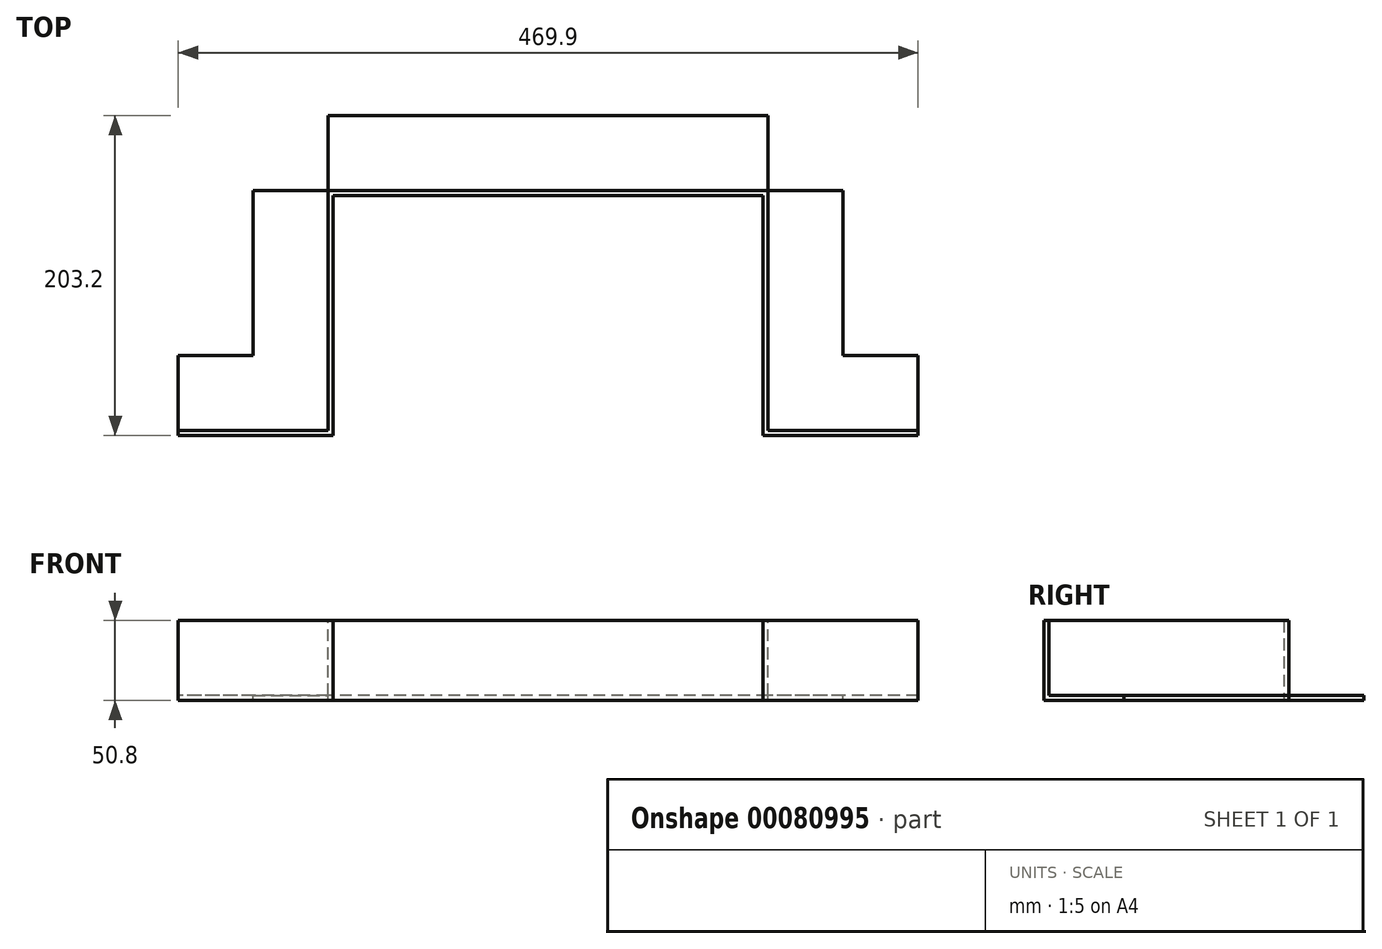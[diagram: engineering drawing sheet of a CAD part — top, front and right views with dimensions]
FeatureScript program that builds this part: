
annotation { "Feature Type Name" : "Feature", "Feature Type Description" : "" }
export const myFeature = defineFeature(function(context is Context, id is Id, definition is map)
    precondition{}
    {
        {
            var Q0;
            Q0=qCreatedBy(makeId("Right.planeOp"),FACE);
            var sketch = newSketch(context, id + "F0", { "sketchPlane" : qUnion([Q0])});
            skLineSegment(sketch, "E0", {"start": v(0, 0) * mm, "end": v(50.8, 0) * mm});
            skLineSegment(sketch, "E1", {"start": v(50.8, 0) * mm, "end": v(50.8, 3.18) * mm});
            skLineSegment(sketch, "E2", {"start": v(50.8, 3.18) * mm, "end": v(3.18, 3.17) * mm});
            skLineSegment(sketch, "E3", {"start": v(3.17, 3.17) * mm, "end": v(3.17, 50.8) * mm});
            skLineSegment(sketch, "E4", {"start": v(3.17, 50.8) * mm, "end": v(0, 50.8) * mm});
            skLineSegment(sketch, "E5", {"start": v(0, 50.8) * mm, "end": v(0, 0) * mm});
            skSolve(sketch);
        }
        {
            var Q0;
            Q0=qCreatedBy(makeId("Top.planeOp"),FACE);
            var sketch = newSketch(context, id + "F1", { "sketchPlane" : qUnion([Q0])});
            skLineSegment(sketch, "E6", {"start": v(0, 0) * mm, "end": v(-98.43, 0) * mm});
            skLineSegment(sketch, "E7", {"start": v(-98.43, 0) * mm, "end": v(-98.43, 152.4) * mm});
            skLineSegment(sketch, "E8", {"start": v(-98.43, 152.4) * mm, "end": v(-371.47, 152.4) * mm});
            skLineSegment(sketch, "E9", {"start": v(-371.47, 152.4) * mm, "end": v(-371.47, 0) * mm});
            skLineSegment(sketch, "E10", {"start": v(-371.47, 0) * mm, "end": v(-469.9, 0) * mm});
            skSolve(sketch);
        }
        {
            var Q0;
            Q0=makeQuery(id+"F0.imprint","IMPRINT",FACE,{"disambiguationData":[TD([[makeQuery(id+"F0.imprint","IMPRINT",EDGE,{"derivedFrom":sQuery(id+"F0.wireOp",EDGE,"E0")}),1.0]])]});
            var Q1;
            Q1=sQuery(id+"F1.wireOp",EDGE,"E6");
            var Q2;
            Q2=sQuery(id+"F1.wireOp",EDGE,"E7");
            var Q3;
            Q3=sQuery(id+"F1.wireOp",EDGE,"E8");
            var Q4;
            Q4=sQuery(id+"F1.wireOp",EDGE,"E9");
            var Q5;
            Q5=sQuery(id+"F1.wireOp",EDGE,"E10");
            sweep(context, id + "F2", {"profiles" : qUnion([Q0]), "path" : qUnion([Q1, Q2, Q3, Q4, Q5])});
        }
        {
            var Q0;
            Q0=makeQuery(id+"F2.opSweep","SWEPT_FACE",FACE,{"disambiguationData":[OSD([sQuery(id+"F0.wireOp",EDGE,"E2"),sQuery(id+"F1.wireOp",EDGE,"E6")])]});
            var sketch = newSketch(context, id + "F3", { "sketchPlane" : qUnion([Q0])});
            skLineSegment(sketch, "E11.bottom", {"start": v(-47.62, 203.2) * mm, "end": v(-95.25, 203.2) * mm});
            skLineSegment(sketch, "E11.top", {"start": v(-47.62, 155.58) * mm, "end": v(-95.25, 155.58) * mm});
            skLineSegment(sketch, "E11.left", {"start": v(-47.62, 203.2) * mm, "end": v(-47.62, 155.58) * mm});
            skLineSegment(sketch, "E11.right", {"start": v(-95.25, 203.2) * mm, "end": v(-95.25, 155.58) * mm});
            skLineSegment(sketch, "E12.bottom", {"start": v(-422.27, 203.2) * mm, "end": v(-374.65, 203.2) * mm});
            skLineSegment(sketch, "E12.top", {"start": v(-422.27, 155.57) * mm, "end": v(-374.65, 155.57) * mm});
            skLineSegment(sketch, "E12.left", {"start": v(-422.27, 203.2) * mm, "end": v(-422.27, 155.57) * mm});
            skLineSegment(sketch, "E12.right", {"start": v(-374.65, 203.2) * mm, "end": v(-374.65, 155.57) * mm});
            skSolve(sketch);
        }
        {
            var Q0;
            Q0=makeQuery(id+"F3.imprint","IMPRINT",FACE,{"disambiguationData":[TD([[makeQuery(id+"F3.imprint","IMPRINT",EDGE,{"derivedFrom":sQuery(id+"F3.wireOp",EDGE,"E12.bottom")}),1.0]])]});
            var Q1;
            Q1=makeQuery(id+"F3.imprint","IMPRINT",FACE,{"disambiguationData":[TD([[makeQuery(id+"F3.imprint","IMPRINT",EDGE,{"derivedFrom":sQuery(id+"F3.wireOp",EDGE,"E11.bottom")}),1.0]])]});
            extrude(context, id + "F4", {"entities" : qUnion([Q0, Q1]), "operationType" : NewBodyOperationType.REMOVE, "oppositeDirection" : true, "depth" : 25.4 * mm});
        }
    });
